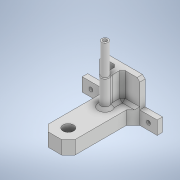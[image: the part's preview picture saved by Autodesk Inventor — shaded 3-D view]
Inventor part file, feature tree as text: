
AUTODESK INVENTOR PART (.ipt)
format: ipt  version: 2022 (Build 260153000, 153)  size: 392,192 bytes
history: native  units: mm
features: sketch x7, extrude x7, chamfer x5, hole x2, other x1
ambient origin geometry x8: Origin, YZ Plane, XZ Plane, XY Plane, X Axis, Y Axis, Z Axis, Center Point
bodies: Body1 (feature_tree)
feature tree (22):
  other  "Sólido1"
  sketch  "Esboço1"  dims[d0=56.0mm d1=10.0mm]
  extrude  "Extrusão1"  Depth=10.0mm
  extrude  "Extrusão2"  Depth=4.0mm TaperAngle=0.0deg
  chamfer  "Chanfro1"  Distance=52.426mm
  hole  "Furo1"  [1 undecoded]
  hole  "Furo2"  [1 undecoded]
  extrude  "Extrusão3"  TaperAngle=0.0deg  [1 undecoded]
  extrude  "Extrusão4"  Depth=20.0mm TaperAngle=0.0deg
  extrude  "Extrusão5"  Depth=10.0mm TaperAngle=45.0deg
  chamfer  "Chanfro2"  Distance=1.0mm Angle=45.0deg
  chamfer  "Chanfro3"  Distance=5.0mm
  sketch  "Esboço7"  dims[d27=41.0mm d28=0.0mm d29=0.0mm d30=0.0mm d33=20.0mm d34=0.0mm d35=2.0mm d36=2.0mm d37=45.0deg d38=1.0mm d39=2.0mm d40=45.0deg d41=5.0mm d42=6.2mm d43=10.0mm d44=0.0mm d45=2.0mm d46=0.0mm d47=0.5mm d48=2.0mm d49=45.0deg d50=2.0mm d51=2.0mm d52=45.0deg]
  extrude  "Extrusão6"  Depth=10.0mm
  extrude  "Extrusão7"  Depth=10.0mm TaperAngle=0.0deg
  chamfer  "Chanfro4"  Distance=2.0mm
  chamfer  "Chanfro5"  Distance=0.5mm Angle=45.0deg
  sketch  "Esboço2"  dims[d2=20.0mm d3=4.0mm d4=0.0mm d5=52.426mm d6=0.0mm]
  sketch  "Esboço3"  dims[d7=5.0mm d8=2.0mm d9=45.0deg]
  sketch  "Esboço4"  dims[d10=8.0mm d11=6.0mm d12=4.0mm d13=2.0mm d14=90.0deg d15=8.0mm d16=20.594885mm]
  sketch  "Esboço5"  dims[d17=3.0mm d18=6.0mm d19=4.0mm d20=2.0mm d21=90.0deg d22=8.0mm d23=20.594885mm d24=10.0mm]
  sketch  "Esboço6"  dims[d25=3.0mm d26=6.0mm]
note: 3 required parameter values undecoded (feature->parameter linkage not recoverable at this tier; creation-order binding heuristic only, values carry confidence <= 0.55)
